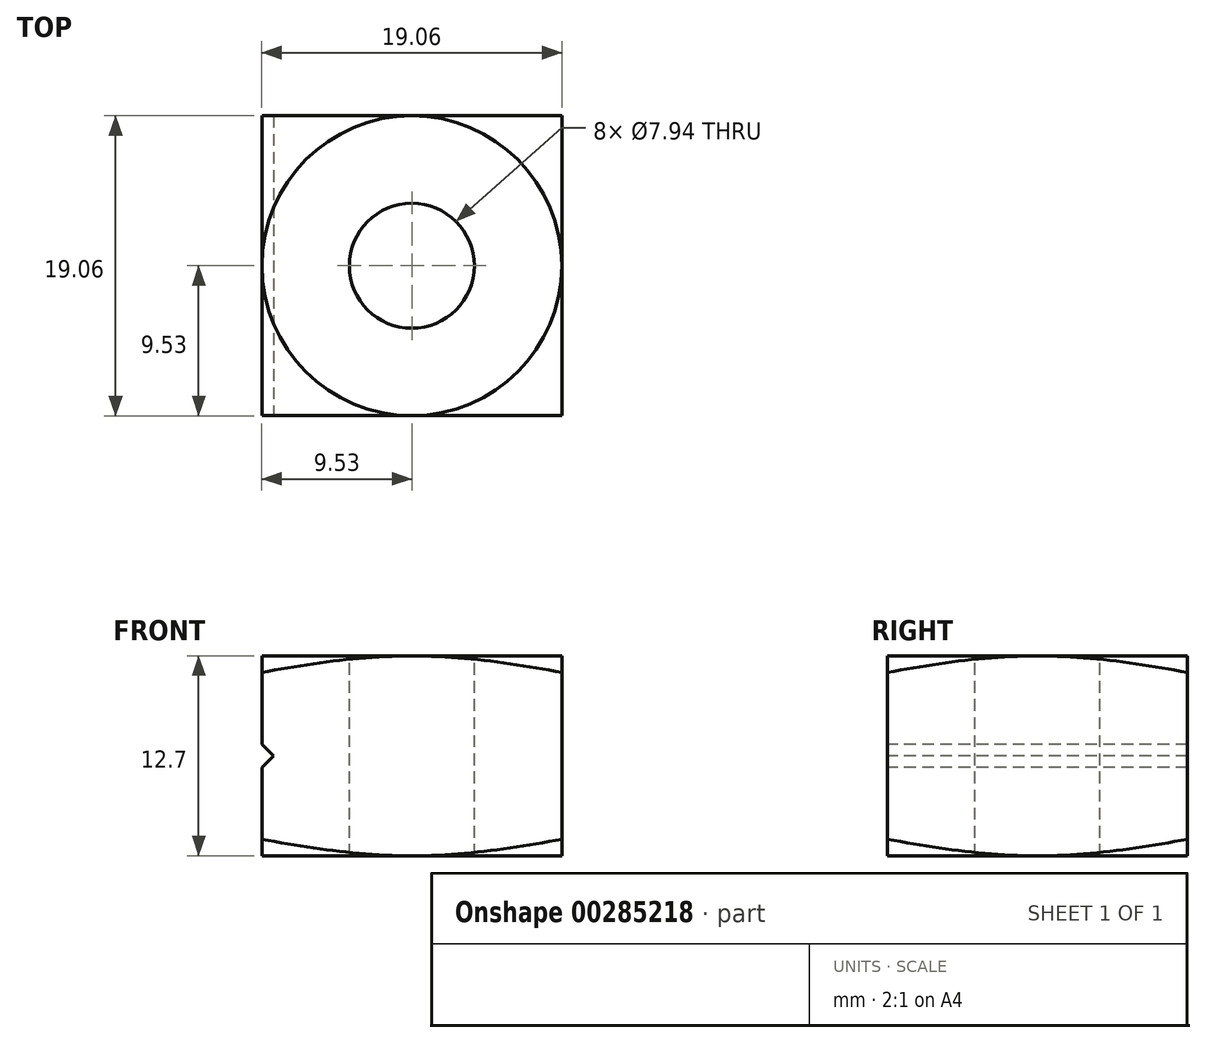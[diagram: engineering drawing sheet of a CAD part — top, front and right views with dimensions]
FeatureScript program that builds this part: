
annotation { "Feature Type Name" : "Feature", "Feature Type Description" : "" }
export const myFeature = defineFeature(function(context is Context, id is Id, definition is map)
    precondition{}
    {
        {
            var Q0;
            Q0=qCreatedBy(makeId("Top.planeOp"),FACE);
            var sketch = newSketch(context, id + "F0", { "sketchPlane" : qUnion([Q0])});
            skLineSegment(sketch, "E0.bottom", {"start": v(9.52, -9.52) * mm, "end": v(-9.53, -9.52) * mm});
            skLineSegment(sketch, "E0.top", {"start": v(9.52, 9.53) * mm, "end": v(-9.53, 9.53) * mm});
            skLineSegment(sketch, "E0.left", {"start": v(9.52, -9.52) * mm, "end": v(9.52, 9.53) * mm});
            skLineSegment(sketch, "E0.right", {"start": v(-9.53, -9.52) * mm, "end": v(-9.53, 9.52) * mm});
            skPoint(sketch, "E0.middle", {"position": v(0, 0) * mm});
            skSolve(sketch);
        }
        {
            var Q0;
            Q0 = qSketchRegion(id + "F0", true);
            extrude(context, id + "F1", {"entities" : qUnion([Q0]), "depth" : 12.7 * mm});
        }
        {
            var Q0;
            Q0=makeQuery(id+"F1.opExtrude","CAP_FACE",FACE,{"disambiguationData":[OSD([sQuery(id+"F0.wireOp",EDGE,"E0.bottom"),sQuery(id+"F0.wireOp",EDGE,"E0.top"),sQuery(id+"F0.wireOp",EDGE,"E0.left"),sQuery(id+"F0.wireOp",EDGE,"E0.right")])],"isStart":false});
            var sketch = newSketch(context, id + "F2", { "sketchPlane" : qUnion([Q0])});
            skCircle(sketch, "E1", {"center": v(0, 0) * mm, "radius": 9.53 * mm});
            skCircle(sketch, "E2", {"center": v(0, 0) * mm, "radius": 3.97 * mm});
            skSolve(sketch);
        }
        {
            var Q0;
            Q0=makeQuery(id+"F2.imprint","IMPRINT",FACE,{"disambiguationData":[TD([[makeQuery(id+"F2.imprint","IMPRINT",EDGE,{"derivedFrom":sQuery(id+"F2.wireOp",EDGE,"E2")}),1.0]])]});
            var Q1;
            Q1=sQuery(id+"F2.wireOp",EDGE,"E2");
            extrude(context, id + "F3", {"entities" : qUnion([Q0]), "operationType" : NewBodyOperationType.REMOVE, "surfaceEntities" : qUnion([Q1]), "endBound" : BoundingType.THROUGH_ALL, "oppositeDirection" : true, "depth" : 25.4 * mm});
        }
        {
            var Q0;
            Q0=qCreatedBy(makeId("Right.planeOp"),FACE);
            var sketch = newSketch(context, id + "F4", { "sketchPlane" : qUnion([Q0])});
            skLineSegment(sketch, "E3.0", {"start": v(-9.53, 12.7) * mm, "end": v(9.53, 12.7) * mm});
            skLineSegment(sketch, "E4.0", {"start": v(9.53, 12.7) * mm, "end": v(9.53, 0) * mm});
            skLineSegment(sketch, "E5", {"start": v(9.53, 12.7) * mm, "end": v(24.77, 12.7) * mm});
            skLineSegment(sketch, "E6", {"start": v(24.77, 12.7) * mm, "end": v(24.77, 8.62) * mm});
            skLineSegment(sketch, "E7", {"start": v(9.53, 12.7) * mm, "end": v(24.77, 8.62) * mm});
            skSolve(sketch);
        }
        {
            var Q0;
            Q0=makeQuery(id+"F4.imprint","IMPRINT",FACE,{"disambiguationData":[TD([[makeQuery(id+"F4.imprint","IMPRINT",EDGE,{"derivedFrom":sQuery(id+"F4.wireOp",EDGE,"E5")}),-1.0]])]});
            var Q1;
            Q1=sQuery(id+"F2.wireOp",EDGE,"E1");
            revolve(context, id + "F5", {"operationType" : NewBodyOperationType.REMOVE, "entities" : qUnion([Q0]), "axis" : qUnion([Q1]), "revolveType" : RevolveType.FULL, "oppositeDirection" : true});
        }
        {
            var Q0;
            Q0=makeQuery(id+"F1.opExtrude","CAP_FACE",FACE,{"disambiguationData":[OSD([sQuery(id+"F0.wireOp",EDGE,"E0.bottom"),sQuery(id+"F0.wireOp",EDGE,"E0.top"),sQuery(id+"F0.wireOp",EDGE,"E0.left"),sQuery(id+"F0.wireOp",EDGE,"E0.right")])],"isStart":true});
            var sketch = newSketch(context, id + "F6", { "sketchPlane" : qUnion([Q0])});
            skCircle(sketch, "E8.0", {"center": v(0, 0) * mm, "radius": 9.53 * mm});
            skSolve(sketch);
        }
        {
            var Q0;
            Q0=qCreatedBy(makeId("Right.planeOp"),FACE);
            var sketch = newSketch(context, id + "F7", { "sketchPlane" : qUnion([Q0])});
            skLineSegment(sketch, "E9.0", {"start": v(-9.53, 0) * mm, "end": v(9.53, 0) * mm});
            skLineSegment(sketch, "E10", {"start": v(-9.53, 0) * mm, "end": v(-22.83, 0) * mm});
            skLineSegment(sketch, "E11", {"start": v(-22.83, 0) * mm, "end": v(-22.83, 3.57) * mm});
            skLineSegment(sketch, "E12", {"start": v(-22.83, 3.57) * mm, "end": v(-9.53, 0) * mm});
            skSolve(sketch);
        }
        {
            var Q0;
            Q0=makeQuery(id+"F7.imprint","IMPRINT",FACE,{"disambiguationData":[TD([[makeQuery(id+"F7.imprint","IMPRINT",EDGE,{"derivedFrom":sQuery(id+"F7.wireOp",EDGE,"E10")}),-1.0]])]});
            var Q1;
            Q1=sQuery(id+"F6.wireOp",EDGE,"E8.0");
            revolve(context, id + "F8", {"operationType" : NewBodyOperationType.REMOVE, "entities" : qUnion([Q0]), "axis" : qUnion([Q1]), "revolveType" : RevolveType.FULL, "oppositeDirection" : true});
        }
        {
            var Q0;
            Q0=qCreatedBy(makeId("Front.planeOp"),FACE);
            var sketch = newSketch(context, id + "F9", { "sketchPlane" : qUnion([Q0])});
            skLineSegment(sketch, "E13.0.0", {"start": v(-9.53, 11.64) * mm, "end": v(-9.53, 1.06) * mm});
            skFitSpline(sketch, "E13.0.1", {"points": [v(-9.53, 1.06) * mm, v(-7.95, 0.76) * mm, v(-5.57, 0.36) * mm, v(-2.39, 0.05) * mm, v(-0.8, 0) * mm, v(0, 0) * mm]});
            skFitSpline(sketch, "E13.0.2", {"points": [v(0, 0) * mm, v(0.8, 0) * mm, v(2.39, 0.05) * mm, v(4.78, 0.28) * mm, v(7.16, 0.63) * mm, v(8.74, 0.9) * mm, v(9.52, 1.06) * mm]});
            skLineSegment(sketch, "E13.0.3", {"start": v(9.52, 1.06) * mm, "end": v(9.52, 11.64) * mm});
            skFitSpline(sketch, "E13.0.4", {"points": [v(9.52, 11.64) * mm, v(8.74, 11.8) * mm, v(7.16, 12.07) * mm, v(4.78, 12.42) * mm, v(2.39, 12.65) * mm, v(0.8, 12.7) * mm, v(0, 12.7) * mm]});
            skFitSpline(sketch, "E13.0.5", {"points": [v(0, 12.7) * mm, v(-0.8, 12.7) * mm, v(-2.39, 12.65) * mm, v(-5.57, 12.34) * mm, v(-7.95, 11.94) * mm, v(-9.53, 11.64) * mm]});
            skFitSpline(sketch, "E14.0.0", {"points": [v(0, 12.7) * mm, v(-0.8, 12.7) * mm, v(-2.39, 12.65) * mm, v(-5.57, 12.34) * mm, v(-7.95, 11.94) * mm, v(-9.53, 11.64) * mm]});
            skLineSegment(sketch, "E14.0.1", {"start": v(0, 12.7) * mm, "end": v(-9.53, 12.7) * mm});
            skFitSpline(sketch, "E14.0.2", {"points": [v(-9.53, 12.7) * mm, v(-9.53, 12.35) * mm, v(-9.53, 12) * mm, v(-9.53, 11.64) * mm]});
            skLineSegment(sketch, "E15.0.0", {"start": v(-9.53, 0) * mm, "end": v(0, 0) * mm});
            skFitSpline(sketch, "E15.0.1", {"points": [v(0, 0) * mm, v(-0.8, 0) * mm, v(-2.39, 0.05) * mm, v(-5.57, 0.36) * mm, v(-7.95, 0.76) * mm, v(-9.53, 1.06) * mm]});
            skFitSpline(sketch, "E15.0.2", {"points": [v(-9.53, 0) * mm, v(-9.53, 0.35) * mm, v(-9.53, 0.7) * mm, v(-9.53, 1.06) * mm]});
            skFitSpline(sketch, "E16.0.1", {"points": [v(-9.53, 1.06) * mm, v(-7.95, 0.76) * mm, v(-5.57, 0.36) * mm, v(-2.39, 0.05) * mm, v(-0.8, 0) * mm, v(0, 0) * mm]});
            skFitSpline(sketch, "E16.0.2", {"points": [v(0, 0) * mm, v(0.8, 0) * mm, v(2.39, 0.05) * mm, v(4.78, 0.28) * mm, v(7.16, 0.63) * mm, v(8.74, 0.9) * mm, v(9.52, 1.06) * mm]});
            skFitSpline(sketch, "E16.0.4", {"points": [v(9.52, 11.64) * mm, v(8.74, 11.8) * mm, v(7.16, 12.07) * mm, v(4.78, 12.42) * mm, v(2.39, 12.65) * mm, v(0.8, 12.7) * mm, v(0, 12.7) * mm]});
            skFitSpline(sketch, "E16.0.5", {"points": [v(0, 12.7) * mm, v(-0.8, 12.7) * mm, v(-2.39, 12.65) * mm, v(-5.57, 12.34) * mm, v(-7.95, 11.94) * mm, v(-9.53, 11.64) * mm]});
            skLineSegment(sketch, "E17", {"start": v(-9.53, 6.35) * mm, "end": v(-9.53, 5.62) * mm});
            skLineSegment(sketch, "E18", {"start": v(-9.53, 5.62) * mm, "end": v(-8.8, 6.35) * mm});
            skLineSegment(sketch, "E19", {"start": v(-8.8, 6.35) * mm, "end": v(-9.53, 6.35) * mm});
            skLineSegment(sketch, "E20", {"start": v(-8.8, 6.35) * mm, "end": v(-9.53, 7.08) * mm});
            skLineSegment(sketch, "E21", {"start": v(-9.53, 7.08) * mm, "end": v(-9.53, 5.62) * mm});
            skSolve(sketch);
        }
        {
            var Q0;
            {var subQ0=sQuery(id+"F9.wireOp",EDGE,"E18");Q0=makeQuery(id+"F9.imprint","IMPRINT",FACE,{"disambiguationData":[TD([[makeQuery(id+"F9.imprint","IMPRINT",EDGE,{"derivedFrom":subQ0}),1.0]])]});}
            var Q1;
            {var subQ0=sQuery(id+"F9.wireOp",EDGE,"E19");Q1=makeQuery(id+"F9.imprint","IMPRINT",FACE,{"disambiguationData":[TD([[makeQuery(id+"F9.imprint","IMPRINT",EDGE,{"derivedFrom":subQ0}),-1.0]])]});}
            extrude(context, id + "F10", {"entities" : qUnion([Q0, Q1]), "operationType" : NewBodyOperationType.REMOVE, "endBound" : BoundingType.SYMMETRIC, "oppositeDirection" : true, "depth" : 25.4 * mm});
        }
    });
